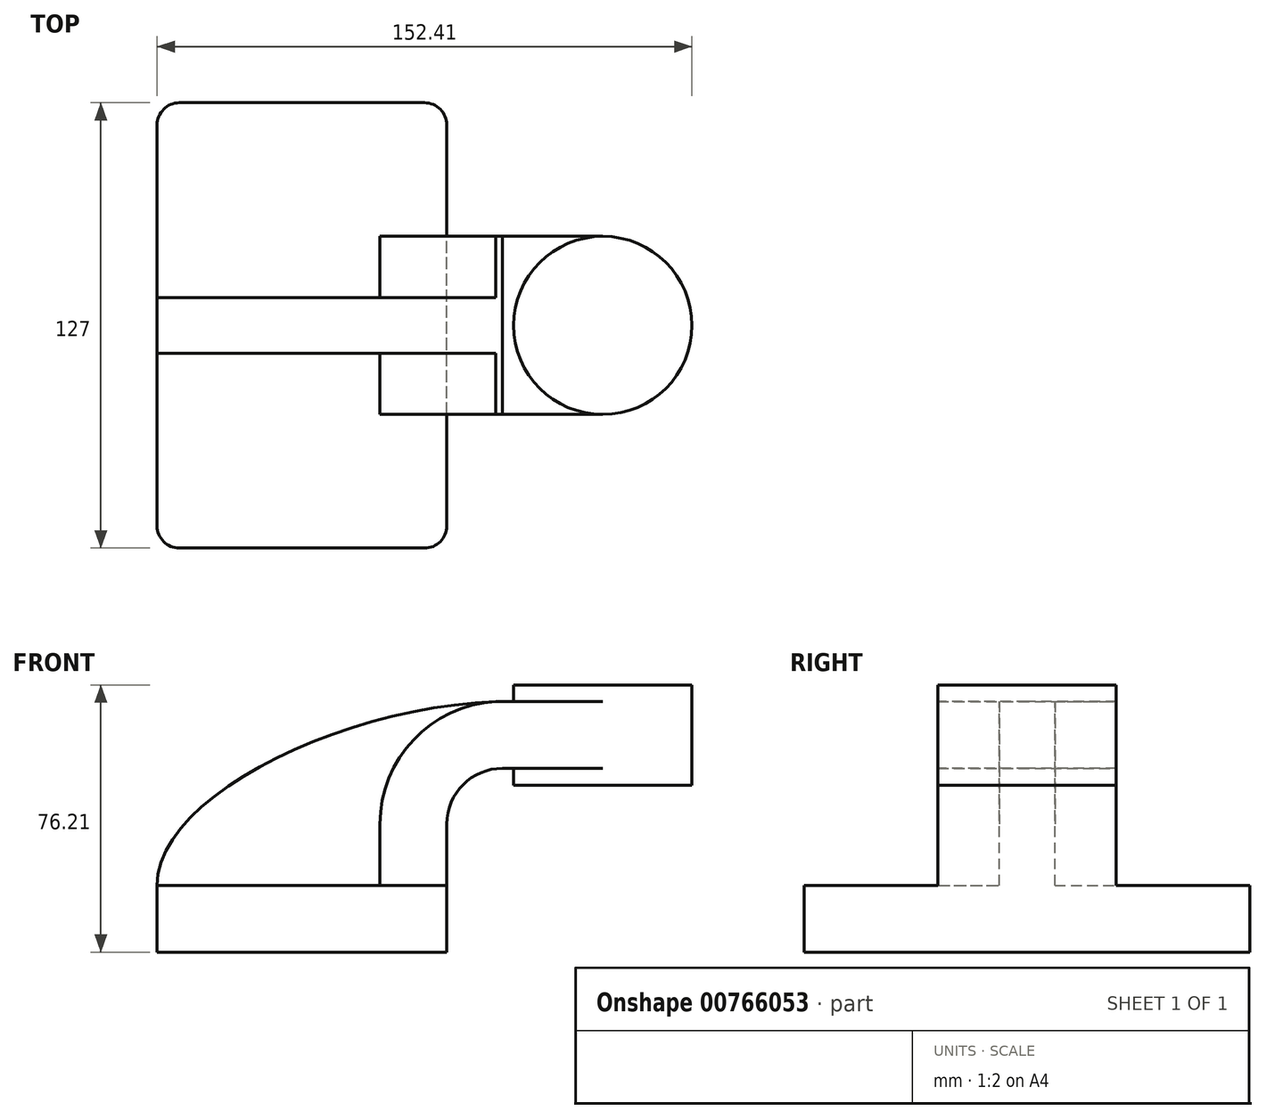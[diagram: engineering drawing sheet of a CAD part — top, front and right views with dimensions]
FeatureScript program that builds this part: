
annotation { "Feature Type Name" : "Feature", "Feature Type Description" : "" }
export const myFeature = defineFeature(function(context is Context, id is Id, definition is map)
    precondition{}
    {
        {
            var Q0;
            Q0=qCreatedBy(makeId("Front.planeOp"),FACE);
            var sketch = newSketch(context, id + "F0", { "sketchPlane" : qUnion([Q0])});
            skLineSegment(sketch, "E0.bottom", {"start": v(-41.28, 9.53) * mm, "end": v(41.27, 9.53) * mm});
            skLineSegment(sketch, "E0.top", {"start": v(-41.28, -9.52) * mm, "end": v(41.28, -9.52) * mm});
            skLineSegment(sketch, "E0.left", {"start": v(-41.28, 9.53) * mm, "end": v(-41.27, -9.52) * mm});
            skLineSegment(sketch, "E0.right", {"start": v(41.27, 9.53) * mm, "end": v(41.28, -9.52) * mm});
            skPoint(sketch, "E0.middle", {"position": v(0, 0) * mm});
            skLineSegment(sketch, "E1.bottom", {"start": v(60.32, 66.68) * mm, "end": v(111.12, 66.68) * mm});
            skLineSegment(sketch, "E1.top", {"start": v(60.32, 38.1) * mm, "end": v(111.12, 38.1) * mm});
            skLineSegment(sketch, "E1.left", {"start": v(60.32, 66.68) * mm, "end": v(60.33, 38.1) * mm});
            skLineSegment(sketch, "E1.right", {"start": v(111.12, 66.68) * mm, "end": v(111.12, 38.1) * mm});
            skPoint(sketch, "E1.middle", {"position": v(85.72, 52.39) * mm});
            skLineSegment(sketch, "E2", {"start": v(41.27, 9.53) * mm, "end": v(41.27, 27) * mm});
            skArc(sketch, "E3", {"start": v(41.27, 27) * mm, "mid": v(45.92, 38.23) * mm, "end": v(57.15, 42.88) * mm});
            skLineSegment(sketch, "E4", {"start": v(57.15, 42.88) * mm, "end": v(85.72, 42.88) * mm});
            skLineSegment(sketch, "E5.0", {"start": v(57.15, 61.93) * mm, "end": v(85.72, 61.93) * mm});
            skArc(sketch, "E5.1", {"start": v(22.22, 27) * mm, "mid": v(32.45, 51.7) * mm, "end": v(57.15, 61.93) * mm});
            skLineSegment(sketch, "E5.2", {"start": v(22.22, 9.52) * mm, "end": v(22.22, 27) * mm});
            skLineSegment(sketch, "E6", {"start": v(85.72, 38.1) * mm, "end": v(85.72, 66.68) * mm});
            skFitSpline(sketch, "E7", {"points": [v(-41.28, 9.53) * mm, v(57.15, 61.93) * mm], "startDerivative": vector(-0.57, 76.54) * mm, "endDerivative": vector(134.27, 2.62) * mm});
            skSolve(sketch);
        }
        {
            var Q0;
            Q0=makeQuery(id+"F0.imprint","IMPRINT",FACE,{"disambiguationData":[TD([[makeQuery(id+"F0.imprint","IMPRINT",EDGE,{"derivedFrom":sQuery(id+"F0.wireOp",EDGE,"E0.top")}),1.0]])]});
            extrude(context, id + "F1", {"entities" : qUnion([Q0]), "endBound" : BoundingType.SYMMETRIC, "depth" : 127 * mm, "offsetDistance" : 25.4 * mm});
        }
        {
            var Q0;
            {var subQ1=sQuery(id+"F0.wireOp",EDGE,"E2");Q0=makeQuery(id+"F0.imprint","IMPRINT",FACE,{"disambiguationData":[TD([[makeQuery(id+"F0.imprint","IMPRINT",EDGE,{"derivedFrom":subQ1}),1.0]])]});}
            var Q1;
            {var subQ0=sQuery(id+"F0.wireOp",EDGE,"E5.0");var subQ1=sQuery(id+"F0.wireOp",EDGE,"E1.left");var subQ2=makeQuery(id+"F0.imprint","INTERSECT",VERTEX,{"derivedFrom":[subQ1,subQ0]});Q1=makeQuery(id+"F0.imprint","IMPRINT",FACE,{"disambiguationData":[TD([[makeQuery(id+"F0.imprint","IMPRINT",EDGE,{"disambiguationData":[TD([[subQ2,-1.0]])],"derivedFrom":subQ1}),1.0]])]});}
            extrude(context, id + "F2", {"entities" : qUnion([Q0, Q1]), "operationType" : NewBodyOperationType.ADD, "endBound" : BoundingType.SYMMETRIC, "depth" : 50.8 * mm, "offsetDistance" : 25.4 * mm});
        }
        {
            var Q0;
            {var subQ3=sQuery(id+"F0.wireOp",EDGE,"E5.2");Q0=makeQuery(id+"F0.imprint","IMPRINT",FACE,{"disambiguationData":[TD([[makeQuery(id+"F0.imprint","IMPRINT",EDGE,{"derivedFrom":subQ3}),1.0]])]});}
            extrude(context, id + "F3", {"entities" : qUnion([Q0]), "operationType" : NewBodyOperationType.ADD, "endBound" : BoundingType.SYMMETRIC, "depth" : 15.88 * mm, "offsetDistance" : 25.4 * mm});
        }
        {
            var Q0;
            {var subQ4=sQuery(id+"F0.wireOp",EDGE,"E1.right");Q0=makeQuery(id+"F0.imprint","IMPRINT",FACE,{"disambiguationData":[TD([[makeQuery(id+"F0.imprint","IMPRINT",EDGE,{"derivedFrom":subQ4}),-1.0]])]});}
            var Q1;
            Q1=sQuery(id+"F0.wireOp",EDGE,"E6");
            revolve(context, id + "F4", {"operationType" : NewBodyOperationType.ADD, "surfaceOperationType" : NewSurfaceOperationType.NEW, "entities" : qUnion([Q0]), "axis" : qUnion([Q1]), "revolveType" : RevolveType.FULL});
        }
        {
            var Q0;
            Q0=makeQuery(id+"F1.opExtrude","CAP_EDGE",EDGE,{"disambiguationData":[OSD([sQuery(id+"F0.wireOp",EDGE,"E0.left")])],"isStart":false});
            var Q1;
            Q1=makeQuery(id+"F1.opExtrude","CAP_EDGE",EDGE,{"disambiguationData":[OSD([sQuery(id+"F0.wireOp",EDGE,"E0.right")])],"isStart":false});
            var Q2;
            Q2=makeQuery(id+"F1.opExtrude","CAP_EDGE",EDGE,{"disambiguationData":[OSD([sQuery(id+"F0.wireOp",EDGE,"E0.left")])],"isStart":true});
            var Q3;
            Q3=makeQuery(id+"F1.opExtrude","CAP_EDGE",EDGE,{"disambiguationData":[OSD([sQuery(id+"F0.wireOp",EDGE,"E0.right")])],"isStart":true});
            fillet(context, id + "F5", {"entities" : qUnion([Q0, Q1, Q2, Q3]), "radius" : 6.35 * mm, "tangentPropagation" : true, "allowEdgeOverflow" : false});
        }
    });
